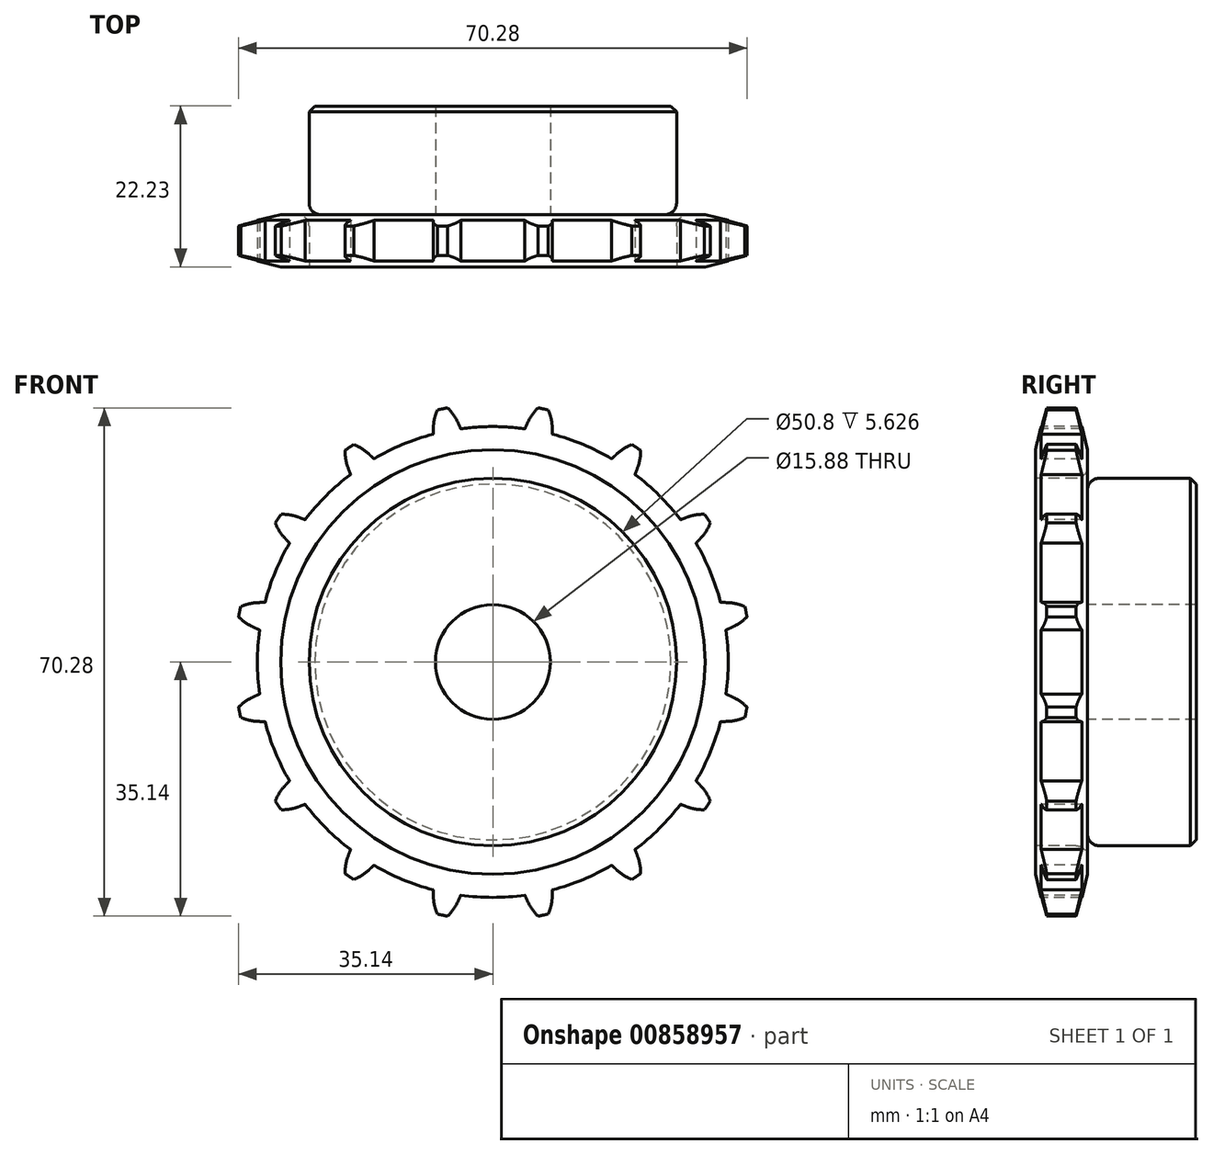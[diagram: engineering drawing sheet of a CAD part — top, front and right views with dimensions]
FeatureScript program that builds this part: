
annotation { "Feature Type Name" : "Feature", "Feature Type Description" : "" }
export const myFeature = defineFeature(function(context is Context, id is Id, definition is map)
    precondition{}
    {
        {
            var Q0;
            Q0=qCreatedBy(makeId("Right.planeOp"),FACE);
            var sketch = newSketch(context, id + "F0", { "sketchPlane" : qUnion([Q0])});
            skLineSegment(sketch, "E0", {"start": v(0, 0) * mm, "end": v(54, 0) * mm, "construction": true});
            skLineSegment(sketch, "E1.bottom", {"start": v(0, 35.69) * mm, "end": v(7.21, 35.69) * mm});
            skLineSegment(sketch, "E1.top", {"start": v(0, 7.94) * mm, "end": v(7.21, 7.94) * mm});
            skLineSegment(sketch, "E1.left", {"start": v(0, 35.69) * mm, "end": v(0, 7.94) * mm});
            skLineSegment(sketch, "E1.right", {"start": v(7.21, 35.69) * mm, "end": v(7.21, 7.94) * mm});
            skLineSegment(sketch, "E2.bottom", {"start": v(0, 7.94) * mm, "end": v(22.23, 7.94) * mm});
            skLineSegment(sketch, "E2.top", {"start": v(0, 25.4) * mm, "end": v(22.23, 25.4) * mm});
            skLineSegment(sketch, "E2.left", {"start": v(0, 7.94) * mm, "end": v(0, 25.4) * mm});
            skLineSegment(sketch, "E2.right", {"start": v(22.23, 7.94) * mm, "end": v(22.23, 25.4) * mm});
            skLineSegment(sketch, "E3.MirrorCS", {"start": v(0, -7.94) * mm, "end": v(7.21, -7.94) * mm});
            skLineSegment(sketch, "E4.MirrorCS", {"start": v(22.23, -7.94) * mm, "end": v(22.23, -25.4) * mm});
            skLineSegment(sketch, "E5.MirrorCS", {"start": v(0, -35.69) * mm, "end": v(0, -7.94) * mm});
            skLineSegment(sketch, "E6.MirrorCS", {"start": v(0, -25.4) * mm, "end": v(22.23, -25.4) * mm});
            skLineSegment(sketch, "E7.MirrorCS", {"start": v(0, -7.94) * mm, "end": v(22.23, -7.94) * mm});
            skLineSegment(sketch, "E8.MirrorCS", {"start": v(0, -7.94) * mm, "end": v(0, -25.4) * mm});
            skLineSegment(sketch, "E9.MirrorCS", {"start": v(0, -35.69) * mm, "end": v(7.21, -35.69) * mm});
            skLineSegment(sketch, "E10.MirrorCS", {"start": v(7.21, -35.69) * mm, "end": v(7.21, -7.94) * mm});
            skSolve(sketch);
        }
        {
            var Q0;
            {var subQ5=sQuery(id+"F0.wireOp",EDGE,"E2.left");Q0=makeQuery(id+"F0.imprint","IMPRINT",FACE,{"disambiguationData":[TD([[makeQuery(id+"F0.imprint","IMPRINT",EDGE,{"derivedFrom":subQ5}),-1.0]])]});}
            var Q1;
            {var subQ5=sQuery(id+"F0.wireOp",EDGE,"E2.right");Q1=makeQuery(id+"F0.imprint","IMPRINT",FACE,{"disambiguationData":[TD([[makeQuery(id+"F0.imprint","IMPRINT",EDGE,{"derivedFrom":subQ5}),1.0]])]});}
            var Q2;
            {var subQ0=sQuery(id+"F0.wireOp",EDGE,"E1.bottom");Q2=makeQuery(id+"F0.imprint","IMPRINT",FACE,{"disambiguationData":[TD([[makeQuery(id+"F0.imprint","IMPRINT",EDGE,{"derivedFrom":subQ0}),-1.0]])]});}
            var Q3;
            Q3=sQuery(id+"F0.wireOp",EDGE,"E0");
            revolve(context, id + "F1", {"surfaceOperationType" : NewSurfaceOperationType.NEW, "entities" : qUnion([Q0, Q1, Q2]), "axis" : qUnion([Q3]), "revolveType" : RevolveType.FULL});
        }
        {
            var Q0;
            Q0=makeQuery(id+"F1.opRevolve","SWEPT_EDGE",EDGE,{"disambiguationData":[OSD([sQuery(id+"F0.wireOp",EDGE,"E1.right"),sQuery(id+"F0.wireOp",EDGE,"E2.top")])]});
            fillet(context, id + "F2", {"entities" : qUnion([Q0]), "radius" : 1.59 * mm, "tangentPropagation" : true, "allowEdgeOverflow" : false});
        }
        {
            var Q0;
            Q0=makeQuery(id+"F1.opRevolve","SWEPT_EDGE",EDGE,{"disambiguationData":[OSD([sQuery(id+"F0.wireOp",EDGE,"E2.top"),sQuery(id+"F0.wireOp",EDGE,"E2.right")])]});
            chamfer(context, id + "F3", {"entities" : qUnion([Q0]), "width" : 0.8 * mm, "tangentPropagation" : true});
        }
        {
            var Q0;
            Q0=makeQuery(id+"F1.opRevolve","SWEPT_EDGE",EDGE,{"disambiguationData":[OSD([sQuery(id+"F0.wireOp",EDGE,"E1.bottom"),sQuery(id+"F0.wireOp",EDGE,"E1.left")])]});
            var Q1;
            Q1=makeQuery(id+"F1.opRevolve","SWEPT_EDGE",EDGE,{"disambiguationData":[OSD([sQuery(id+"F0.wireOp",EDGE,"E1.bottom"),sQuery(id+"F0.wireOp",EDGE,"E1.right")])]});
            chamfer(context, id + "F4", {"entities" : qUnion([Q0, Q1]), "chamferType" : ChamferType.TWO_OFFSETS, "width1" : 6.35 * mm, "oppositeDirection" : false, "width2" : 1.57 * mm, "tangentPropagation" : true});
        }
        {
            var Q0;
            Q0=makeQuery(id+"F1.opRevolve","SWEPT_FACE",FACE,{"disambiguationData":[OSD([sQuery(id+"F0.wireOp",EDGE,"E1.left"),sQuery(id+"F0.wireOp",EDGE,"E2.left")])]});
            var sketch = newSketch(context, id + "F5", { "sketchPlane" : qUnion([Q0])});
            skCircle(sketch, "E11", {"center": v(0, 0) * mm, "radius": 32.55 * mm});
            skLineSegment(sketch, "E12", {"start": v(0, 0) * mm, "end": v(0, 32.55) * mm, "construction": true});
            skLineSegment(sketch, "E13", {"start": v(0, 32.55) * mm, "end": v(36.9, 32.55) * mm, "construction": true});
            skLineSegment(sketch, "E14", {"start": v(0, 32.55) * mm, "end": v(5, 36.56) * mm, "construction": true});
            skLineSegment(sketch, "E15", {"start": v(5, 36.56) * mm, "end": v(-4.46, 32.3) * mm, "construction": true});
            skLineSegment(sketch, "E16", {"start": v(-4.46, 32.3) * mm, "end": v(-4.46, 32.3) * mm});
            skLineSegment(sketch, "E17", {"start": v(0, 0) * mm, "end": v(-7.13, 35.85) * mm, "construction": true});
            skArc(sketch, "E18", {"start": v(-7.13, 35.85) * mm, "mid": v(-15.87, 26.15) * mm, "end": v(-4.82, 33.1) * mm, "construction": true});
            skArc(sketch, "E19", {"start": v(-4.82, 33.1) * mm, "mid": v(-5.78, 34.63) * mm, "end": v(-7.13, 35.85) * mm});
            skLineSegment(sketch, "E20", {"start": v(-4.46, 32.3) * mm, "end": v(-4.82, 33.1) * mm});
            skLineSegment(sketch, "E21.MirrorCS", {"start": v(16.78, 7.56) * mm, "end": v(-7.6, 29.13) * mm, "construction": true});
            skArc(sketch, "E22", {"start": v(-4.46, 32.3) * mm, "mid": v(-3.84, 31.14) * mm, "end": v(-3.1, 30.07) * mm});
            skArc(sketch, "E23", {"start": v(-3.1, 30.07) * mm, "mid": v(13.83, 41.97) * mm, "end": v(-4.46, 32.3) * mm, "construction": true});
            skArc(sketch, "E24.MirrorCS", {"start": v(4.46, 32.3) * mm, "mid": v(3.84, 31.14) * mm, "end": v(3.1, 30.07) * mm});
            skLineSegment(sketch, "E25", {"start": v(-4.82, 33.1) * mm, "end": v(-4.46, 32.3) * mm});
            skArc(sketch, "E26.MirrorCS", {"start": v(-4.46, 32.3) * mm, "mid": v(-4, 31.07) * mm, "end": v(-3.7, 29.8) * mm});
            skArc(sketch, "E27.MirrorCS", {"start": v(-4.82, 33.1) * mm, "mid": v(-5.33, 34.84) * mm, "end": v(-5.34, 36.65) * mm, "construction": true});
            skArc(sketch, "E28.MirrorCS", {"start": v(-4.46, 32.3) * mm, "mid": v(-4, 31.07) * mm, "end": v(-3.7, 29.8) * mm, "construction": true});
            skCircle(sketch, "E29.MirrorC", {"center": v(-7.6, 29.13) * mm, "radius": 3.96 * mm, "construction": true});
            skArc(sketch, "E30.MirrorCS", {"start": v(4.82, 33.1) * mm, "mid": v(5.78, 34.63) * mm, "end": v(7.13, 35.85) * mm});
            skLineSegment(sketch, "E31.MirrorCS", {"start": v(4.82, 33.1) * mm, "end": v(4.46, 32.3) * mm});
            skArc(sketch, "E32", {"start": v(-3.1, 30.07) * mm, "mid": v(-1.31, 28.81) * mm, "end": v(0.86, 28.68) * mm});
            skArc(sketch, "E33", {"start": v(3.1, 30.07) * mm, "mid": v(0, 36.51) * mm, "end": v(-3.1, 30.07) * mm, "construction": true});
            skArc(sketch, "E34", {"start": v(0.86, 28.68) * mm, "mid": v(2.1, 29.19) * mm, "end": v(3.1, 30.07) * mm});
            skArc(sketch, "E35.1.0", {"start": v(-26.26, -20.72) * mm, "mid": v(-27.1, -22.33) * mm, "end": v(-27.48, -24.1) * mm});
            skLineSegment(sketch, "E35.1.1", {"start": v(-26.26, -20.72) * mm, "end": v(-25.74, -20) * mm});
            skArc(sketch, "E35.1.2", {"start": v(-25.74, -20) * mm, "mid": v(-25.05, -18.9) * mm, "end": v(-24.5, -17.71) * mm});
            skArc(sketch, "E35.2.0", {"start": v(31.07, -12.38) * mm, "mid": v(32.89, -12.3) * mm, "end": v(34.61, -11.75) * mm});
            skLineSegment(sketch, "E35.2.1", {"start": v(31.07, -12.38) * mm, "end": v(30.2, -12.3) * mm});
            skArc(sketch, "E35.2.2", {"start": v(30.2, -12.3) * mm, "mid": v(28.9, -12.24) * mm, "end": v(27.59, -12.36) * mm});
            skArc(sketch, "E36.1.0", {"start": v(-17.12, 28.74) * mm, "mid": v(-18.25, 30.15) * mm, "end": v(-18.96, 31.82) * mm, "construction": true});
            skArc(sketch, "E36.1.1", {"start": v(-16.48, 28.14) * mm, "mid": v(-15.58, 27.18) * mm, "end": v(-14.81, 26.12) * mm, "construction": true});
            skArc(sketch, "E36.1.2", {"start": v(-17.12, 28.74) * mm, "mid": v(-18.6, 29.79) * mm, "end": v(-20.3, 30.4) * mm});
            skLineSegment(sketch, "E36.1.3", {"start": v(-17.12, 28.74) * mm, "end": v(-16.48, 28.14) * mm});
            skArc(sketch, "E36.1.4", {"start": v(-16.48, 28.14) * mm, "mid": v(-15.47, 27.3) * mm, "end": v(-14.36, 26.6) * mm});
            skArc(sketch, "E36.1.5", {"start": v(-14.36, 26.6) * mm, "mid": v(-12.24, 26.12) * mm, "end": v(-10.18, 26.83) * mm});
            skArc(sketch, "E36.1.6", {"start": v(-10.18, 26.83) * mm, "mid": v(-9.23, 27.77) * mm, "end": v(-8.65, 28.96) * mm});
            skArc(sketch, "E36.1.7", {"start": v(-8.24, 31.55) * mm, "mid": v(-8.37, 30.24) * mm, "end": v(-8.65, 28.96) * mm});
            skLineSegment(sketch, "E36.1.8", {"start": v(-8.22, 32.42) * mm, "end": v(-8.24, 31.55) * mm});
            skArc(sketch, "E36.1.9", {"start": v(-8.22, 32.42) * mm, "mid": v(-7.91, 34.21) * mm, "end": v(-7.13, 35.85) * mm});
            skArc(sketch, "E36.2.0", {"start": v(-26.8, 20) * mm, "mid": v(-28.4, 20.87) * mm, "end": v(-29.7, 22.14) * mm, "construction": true});
            skArc(sketch, "E36.2.1", {"start": v(-26, 19.69) * mm, "mid": v(-24.8, 19.15) * mm, "end": v(-23.68, 18.46) * mm, "construction": true});
            skArc(sketch, "E36.2.2", {"start": v(-26.8, 20) * mm, "mid": v(-28.58, 20.4) * mm, "end": v(-30.4, 20.3) * mm});
            skLineSegment(sketch, "E36.2.3", {"start": v(-26.8, 20) * mm, "end": v(-26, 19.69) * mm});
            skArc(sketch, "E36.2.4", {"start": v(-26, 19.69) * mm, "mid": v(-24.74, 19.3) * mm, "end": v(-23.45, 19.08) * mm});
            skArc(sketch, "E36.2.5", {"start": v(-23.45, 19.08) * mm, "mid": v(-21.3, 19.45) * mm, "end": v(-19.67, 20.9) * mm});
            skArc(sketch, "E36.2.6", {"start": v(-19.67, 20.9) * mm, "mid": v(-19.16, 22.12) * mm, "end": v(-19.08, 23.45) * mm});
            skArc(sketch, "E36.2.7", {"start": v(-19.69, 26) * mm, "mid": v(-19.3, 24.74) * mm, "end": v(-19.08, 23.45) * mm});
            skLineSegment(sketch, "E36.2.8", {"start": v(-20, 26.8) * mm, "end": v(-19.69, 26) * mm});
            skArc(sketch, "E36.2.9", {"start": v(-20, 26.8) * mm, "mid": v(-20.4, 28.58) * mm, "end": v(-20.3, 30.4) * mm});
            skArc(sketch, "E36.3.0", {"start": v(-32.42, 8.22) * mm, "mid": v(-34.23, 8.41) * mm, "end": v(-35.9, 9.1) * mm, "construction": true});
            skArc(sketch, "E36.3.1", {"start": v(-31.55, 8.24) * mm, "mid": v(-30.24, 8.2) * mm, "end": v(-28.94, 8) * mm, "construction": true});
            skArc(sketch, "E36.3.2", {"start": v(-32.42, 8.22) * mm, "mid": v(-34.21, 7.91) * mm, "end": v(-35.85, 7.13) * mm});
            skLineSegment(sketch, "E36.3.3", {"start": v(-32.42, 8.22) * mm, "end": v(-31.55, 8.24) * mm});
            skArc(sketch, "E36.3.4", {"start": v(-31.55, 8.24) * mm, "mid": v(-30.24, 8.37) * mm, "end": v(-28.96, 8.65) * mm});
            skArc(sketch, "E36.3.5", {"start": v(-28.96, 8.65) * mm, "mid": v(-27.12, 9.81) * mm, "end": v(-26.17, 11.77) * mm});
            skArc(sketch, "E36.3.6", {"start": v(-26.17, 11.77) * mm, "mid": v(-26.16, 13.1) * mm, "end": v(-26.6, 14.36) * mm});
            skArc(sketch, "E36.3.7", {"start": v(-28.14, 16.48) * mm, "mid": v(-27.3, 15.47) * mm, "end": v(-26.6, 14.36) * mm});
            skLineSegment(sketch, "E36.3.8", {"start": v(-28.74, 17.12) * mm, "end": v(-28.14, 16.48) * mm});
            skArc(sketch, "E36.3.9", {"start": v(-28.74, 17.12) * mm, "mid": v(-29.79, 18.6) * mm, "end": v(-30.4, 20.3) * mm});
            skArc(sketch, "E36.4.0", {"start": v(-33.1, -4.82) * mm, "mid": v(-34.84, -5.33) * mm, "end": v(-36.65, -5.34) * mm, "construction": true});
            skArc(sketch, "E36.4.1", {"start": v(-32.3, -4.46) * mm, "mid": v(-31.07, -4) * mm, "end": v(-29.8, -3.7) * mm, "construction": true});
            skArc(sketch, "E36.4.2", {"start": v(-33.1, -4.82) * mm, "mid": v(-34.63, -5.78) * mm, "end": v(-35.85, -7.13) * mm});
            skLineSegment(sketch, "E36.4.3", {"start": v(-33.1, -4.82) * mm, "end": v(-32.3, -4.46) * mm});
            skArc(sketch, "E36.4.4", {"start": v(-32.3, -4.46) * mm, "mid": v(-31.14, -3.84) * mm, "end": v(-30.07, -3.1) * mm});
            skArc(sketch, "E36.4.5", {"start": v(-30.07, -3.1) * mm, "mid": v(-28.81, -1.31) * mm, "end": v(-28.68, 0.86) * mm});
            skArc(sketch, "E36.4.6", {"start": v(-28.68, 0.86) * mm, "mid": v(-29.19, 2.1) * mm, "end": v(-30.07, 3.1) * mm});
            skArc(sketch, "E36.4.7", {"start": v(-32.3, 4.46) * mm, "mid": v(-31.14, 3.84) * mm, "end": v(-30.07, 3.1) * mm});
            skLineSegment(sketch, "E36.4.8", {"start": v(-33.1, 4.82) * mm, "end": v(-32.3, 4.46) * mm});
            skArc(sketch, "E36.4.9", {"start": v(-33.1, 4.82) * mm, "mid": v(-34.63, 5.78) * mm, "end": v(-35.85, 7.13) * mm});
            skArc(sketch, "E36.5.0", {"start": v(-28.74, -17.12) * mm, "mid": v(-30.15, -18.25) * mm, "end": v(-31.82, -18.96) * mm, "construction": true});
            skArc(sketch, "E36.5.1", {"start": v(-28.14, -16.48) * mm, "mid": v(-27.18, -15.58) * mm, "end": v(-26.12, -14.81) * mm, "construction": true});
            skArc(sketch, "E36.5.2", {"start": v(-28.74, -17.12) * mm, "mid": v(-29.79, -18.6) * mm, "end": v(-30.4, -20.3) * mm});
            skLineSegment(sketch, "E36.5.3", {"start": v(-28.74, -17.12) * mm, "end": v(-28.14, -16.48) * mm});
            skArc(sketch, "E36.5.4", {"start": v(-28.14, -16.48) * mm, "mid": v(-27.3, -15.47) * mm, "end": v(-26.6, -14.36) * mm});
            skArc(sketch, "E36.5.5", {"start": v(-26.6, -14.36) * mm, "mid": v(-26.12, -12.24) * mm, "end": v(-26.83, -10.18) * mm});
            skArc(sketch, "E36.5.6", {"start": v(-26.83, -10.18) * mm, "mid": v(-27.77, -9.23) * mm, "end": v(-28.96, -8.65) * mm});
            skArc(sketch, "E36.5.7", {"start": v(-31.55, -8.24) * mm, "mid": v(-30.24, -8.37) * mm, "end": v(-28.96, -8.65) * mm});
            skLineSegment(sketch, "E36.5.8", {"start": v(-32.42, -8.22) * mm, "end": v(-31.55, -8.24) * mm});
            skArc(sketch, "E36.5.9", {"start": v(-32.42, -8.22) * mm, "mid": v(-34.21, -7.91) * mm, "end": v(-35.85, -7.13) * mm});
            skArc(sketch, "E36.6.0", {"start": v(-20, -26.8) * mm, "mid": v(-20.87, -28.4) * mm, "end": v(-22.14, -29.7) * mm, "construction": true});
            skArc(sketch, "E36.6.1", {"start": v(-19.69, -26) * mm, "mid": v(-19.15, -24.8) * mm, "end": v(-18.46, -23.68) * mm, "construction": true});
            skArc(sketch, "E36.6.2", {"start": v(-20, -26.8) * mm, "mid": v(-20.4, -28.58) * mm, "end": v(-20.3, -30.4) * mm});
            skLineSegment(sketch, "E36.6.3", {"start": v(-20, -26.8) * mm, "end": v(-19.69, -26) * mm});
            skArc(sketch, "E36.6.4", {"start": v(-19.69, -26) * mm, "mid": v(-19.3, -24.74) * mm, "end": v(-19.08, -23.45) * mm});
            skArc(sketch, "E36.6.5", {"start": v(-19.08, -23.45) * mm, "mid": v(-19.45, -21.3) * mm, "end": v(-20.9, -19.67) * mm});
            skArc(sketch, "E36.6.6", {"start": v(-20.9, -19.67) * mm, "mid": v(-22.12, -19.16) * mm, "end": v(-23.45, -19.08) * mm});
            skArc(sketch, "E36.6.7", {"start": v(-26, -19.69) * mm, "mid": v(-24.74, -19.3) * mm, "end": v(-23.45, -19.08) * mm});
            skLineSegment(sketch, "E36.6.8", {"start": v(-26.8, -20) * mm, "end": v(-26, -19.69) * mm});
            skArc(sketch, "E36.6.9", {"start": v(-26.8, -20) * mm, "mid": v(-28.58, -20.4) * mm, "end": v(-30.4, -20.3) * mm});
            skArc(sketch, "E36.7.0", {"start": v(-8.22, -32.42) * mm, "mid": v(-8.41, -34.23) * mm, "end": v(-9.1, -35.9) * mm, "construction": true});
            skArc(sketch, "E36.7.1", {"start": v(-8.24, -31.55) * mm, "mid": v(-8.2, -30.24) * mm, "end": v(-8, -28.94) * mm, "construction": true});
            skArc(sketch, "E36.7.2", {"start": v(-8.22, -32.42) * mm, "mid": v(-7.91, -34.21) * mm, "end": v(-7.13, -35.85) * mm});
            skLineSegment(sketch, "E36.7.3", {"start": v(-8.22, -32.42) * mm, "end": v(-8.24, -31.55) * mm});
            skArc(sketch, "E36.7.4", {"start": v(-8.24, -31.55) * mm, "mid": v(-8.37, -30.24) * mm, "end": v(-8.65, -28.96) * mm});
            skArc(sketch, "E36.7.5", {"start": v(-8.65, -28.96) * mm, "mid": v(-9.81, -27.12) * mm, "end": v(-11.77, -26.17) * mm});
            skArc(sketch, "E36.7.6", {"start": v(-11.77, -26.17) * mm, "mid": v(-13.1, -26.16) * mm, "end": v(-14.36, -26.6) * mm});
            skArc(sketch, "E36.7.7", {"start": v(-16.48, -28.14) * mm, "mid": v(-15.47, -27.3) * mm, "end": v(-14.36, -26.6) * mm});
            skLineSegment(sketch, "E36.7.8", {"start": v(-17.12, -28.74) * mm, "end": v(-16.48, -28.14) * mm});
            skArc(sketch, "E36.7.9", {"start": v(-17.12, -28.74) * mm, "mid": v(-18.6, -29.79) * mm, "end": v(-20.3, -30.4) * mm});
            skArc(sketch, "E36.8.0", {"start": v(4.82, -33.1) * mm, "mid": v(5.33, -34.84) * mm, "end": v(5.34, -36.65) * mm, "construction": true});
            skArc(sketch, "E36.8.1", {"start": v(4.46, -32.3) * mm, "mid": v(4, -31.07) * mm, "end": v(3.7, -29.8) * mm, "construction": true});
            skArc(sketch, "E36.8.2", {"start": v(4.82, -33.1) * mm, "mid": v(5.78, -34.63) * mm, "end": v(7.13, -35.85) * mm});
            skLineSegment(sketch, "E36.8.3", {"start": v(4.82, -33.1) * mm, "end": v(4.46, -32.3) * mm});
            skArc(sketch, "E36.8.4", {"start": v(4.46, -32.3) * mm, "mid": v(3.84, -31.14) * mm, "end": v(3.1, -30.07) * mm});
            skArc(sketch, "E36.8.5", {"start": v(3.1, -30.07) * mm, "mid": v(1.31, -28.81) * mm, "end": v(-0.86, -28.68) * mm});
            skArc(sketch, "E36.8.6", {"start": v(-0.86, -28.68) * mm, "mid": v(-2.1, -29.19) * mm, "end": v(-3.1, -30.07) * mm});
            skArc(sketch, "E36.8.7", {"start": v(-4.46, -32.3) * mm, "mid": v(-3.84, -31.14) * mm, "end": v(-3.1, -30.07) * mm});
            skLineSegment(sketch, "E36.8.8", {"start": v(-4.82, -33.1) * mm, "end": v(-4.46, -32.3) * mm});
            skArc(sketch, "E36.8.9", {"start": v(-4.82, -33.1) * mm, "mid": v(-5.78, -34.63) * mm, "end": v(-7.13, -35.85) * mm});
            skArc(sketch, "E36.9.0", {"start": v(17.12, -28.74) * mm, "mid": v(18.25, -30.15) * mm, "end": v(18.96, -31.82) * mm, "construction": true});
            skArc(sketch, "E36.9.1", {"start": v(16.48, -28.14) * mm, "mid": v(15.58, -27.18) * mm, "end": v(14.81, -26.12) * mm, "construction": true});
            skArc(sketch, "E36.9.2", {"start": v(17.12, -28.74) * mm, "mid": v(18.6, -29.79) * mm, "end": v(20.3, -30.4) * mm});
            skLineSegment(sketch, "E36.9.3", {"start": v(17.12, -28.74) * mm, "end": v(16.48, -28.14) * mm});
            skArc(sketch, "E36.9.4", {"start": v(16.48, -28.14) * mm, "mid": v(15.47, -27.3) * mm, "end": v(14.36, -26.6) * mm});
            skArc(sketch, "E36.9.5", {"start": v(14.36, -26.6) * mm, "mid": v(12.24, -26.12) * mm, "end": v(10.18, -26.83) * mm});
            skArc(sketch, "E36.9.6", {"start": v(10.18, -26.83) * mm, "mid": v(9.23, -27.77) * mm, "end": v(8.65, -28.96) * mm});
            skArc(sketch, "E36.9.7", {"start": v(8.24, -31.55) * mm, "mid": v(8.37, -30.24) * mm, "end": v(8.65, -28.96) * mm});
            skLineSegment(sketch, "E36.9.8", {"start": v(8.22, -32.42) * mm, "end": v(8.24, -31.55) * mm});
            skArc(sketch, "E36.9.9", {"start": v(8.22, -32.42) * mm, "mid": v(7.91, -34.21) * mm, "end": v(7.13, -35.85) * mm});
            skArc(sketch, "E36.10.0", {"start": v(26.8, -20) * mm, "mid": v(28.4, -20.87) * mm, "end": v(29.7, -22.14) * mm, "construction": true});
            skArc(sketch, "E36.10.1", {"start": v(26, -19.69) * mm, "mid": v(24.8, -19.15) * mm, "end": v(23.68, -18.46) * mm, "construction": true});
            skArc(sketch, "E36.10.2", {"start": v(26.8, -20) * mm, "mid": v(28.58, -20.4) * mm, "end": v(30.4, -20.3) * mm});
            skLineSegment(sketch, "E36.10.3", {"start": v(26.8, -20) * mm, "end": v(26, -19.69) * mm});
            skArc(sketch, "E36.10.4", {"start": v(26, -19.69) * mm, "mid": v(24.74, -19.3) * mm, "end": v(23.45, -19.08) * mm});
            skArc(sketch, "E36.10.5", {"start": v(23.45, -19.08) * mm, "mid": v(21.3, -19.45) * mm, "end": v(19.67, -20.9) * mm});
            skArc(sketch, "E36.10.6", {"start": v(19.67, -20.9) * mm, "mid": v(19.16, -22.12) * mm, "end": v(19.08, -23.45) * mm});
            skArc(sketch, "E36.10.7", {"start": v(19.69, -26) * mm, "mid": v(19.3, -24.74) * mm, "end": v(19.08, -23.45) * mm});
            skLineSegment(sketch, "E36.10.8", {"start": v(20, -26.8) * mm, "end": v(19.69, -26) * mm});
            skArc(sketch, "E36.10.9", {"start": v(20, -26.8) * mm, "mid": v(20.4, -28.58) * mm, "end": v(20.3, -30.4) * mm});
            skArc(sketch, "E36.11.0", {"start": v(32.42, -8.22) * mm, "mid": v(34.23, -8.41) * mm, "end": v(35.9, -9.1) * mm, "construction": true});
            skArc(sketch, "E36.11.1", {"start": v(31.55, -8.24) * mm, "mid": v(30.24, -8.2) * mm, "end": v(28.94, -8) * mm, "construction": true});
            skArc(sketch, "E36.11.2", {"start": v(32.42, -8.22) * mm, "mid": v(34.21, -7.91) * mm, "end": v(35.85, -7.13) * mm});
            skLineSegment(sketch, "E36.11.3", {"start": v(32.42, -8.22) * mm, "end": v(31.55, -8.24) * mm});
            skArc(sketch, "E36.11.4", {"start": v(31.55, -8.24) * mm, "mid": v(30.24, -8.37) * mm, "end": v(28.96, -8.65) * mm});
            skArc(sketch, "E36.11.5", {"start": v(28.96, -8.65) * mm, "mid": v(27.12, -9.81) * mm, "end": v(26.17, -11.77) * mm});
            skArc(sketch, "E36.11.6", {"start": v(26.17, -11.77) * mm, "mid": v(26.16, -13.1) * mm, "end": v(26.6, -14.36) * mm});
            skArc(sketch, "E36.11.7", {"start": v(28.14, -16.48) * mm, "mid": v(27.3, -15.47) * mm, "end": v(26.6, -14.36) * mm});
            skLineSegment(sketch, "E36.11.8", {"start": v(28.74, -17.12) * mm, "end": v(28.14, -16.48) * mm});
            skArc(sketch, "E36.11.9", {"start": v(28.74, -17.12) * mm, "mid": v(29.79, -18.6) * mm, "end": v(30.4, -20.3) * mm});
            skArc(sketch, "E36.12.0", {"start": v(33.1, 4.82) * mm, "mid": v(34.84, 5.33) * mm, "end": v(36.65, 5.34) * mm, "construction": true});
            skArc(sketch, "E36.12.1", {"start": v(32.3, 4.46) * mm, "mid": v(31.07, 4) * mm, "end": v(29.8, 3.7) * mm, "construction": true});
            skArc(sketch, "E36.12.2", {"start": v(33.1, 4.82) * mm, "mid": v(34.63, 5.78) * mm, "end": v(35.85, 7.13) * mm});
            skLineSegment(sketch, "E36.12.3", {"start": v(33.1, 4.82) * mm, "end": v(32.3, 4.46) * mm});
            skArc(sketch, "E36.12.4", {"start": v(32.3, 4.46) * mm, "mid": v(31.14, 3.84) * mm, "end": v(30.07, 3.1) * mm});
            skArc(sketch, "E36.12.5", {"start": v(30.07, 3.1) * mm, "mid": v(28.81, 1.31) * mm, "end": v(28.68, -0.86) * mm});
            skArc(sketch, "E36.12.6", {"start": v(28.68, -0.86) * mm, "mid": v(29.19, -2.1) * mm, "end": v(30.07, -3.1) * mm});
            skArc(sketch, "E36.12.7", {"start": v(32.3, -4.46) * mm, "mid": v(31.14, -3.84) * mm, "end": v(30.07, -3.1) * mm});
            skLineSegment(sketch, "E36.12.8", {"start": v(33.1, -4.82) * mm, "end": v(32.3, -4.46) * mm});
            skArc(sketch, "E36.12.9", {"start": v(33.1, -4.82) * mm, "mid": v(34.63, -5.78) * mm, "end": v(35.85, -7.13) * mm});
            skArc(sketch, "E36.13.0", {"start": v(28.74, 17.12) * mm, "mid": v(30.15, 18.25) * mm, "end": v(31.82, 18.96) * mm, "construction": true});
            skArc(sketch, "E36.13.1", {"start": v(28.14, 16.48) * mm, "mid": v(27.18, 15.58) * mm, "end": v(26.12, 14.81) * mm, "construction": true});
            skArc(sketch, "E36.13.2", {"start": v(28.74, 17.12) * mm, "mid": v(29.79, 18.6) * mm, "end": v(30.4, 20.3) * mm});
            skLineSegment(sketch, "E36.13.3", {"start": v(28.74, 17.12) * mm, "end": v(28.14, 16.48) * mm});
            skArc(sketch, "E36.13.4", {"start": v(28.14, 16.48) * mm, "mid": v(27.3, 15.47) * mm, "end": v(26.6, 14.36) * mm});
            skArc(sketch, "E36.13.5", {"start": v(26.6, 14.36) * mm, "mid": v(26.12, 12.24) * mm, "end": v(26.83, 10.18) * mm});
            skArc(sketch, "E36.13.6", {"start": v(26.83, 10.18) * mm, "mid": v(27.77, 9.23) * mm, "end": v(28.96, 8.65) * mm});
            skArc(sketch, "E36.13.7", {"start": v(31.55, 8.24) * mm, "mid": v(30.24, 8.37) * mm, "end": v(28.96, 8.65) * mm});
            skLineSegment(sketch, "E36.13.8", {"start": v(32.42, 8.22) * mm, "end": v(31.55, 8.24) * mm});
            skArc(sketch, "E36.13.9", {"start": v(32.42, 8.22) * mm, "mid": v(34.21, 7.91) * mm, "end": v(35.85, 7.13) * mm});
            skArc(sketch, "E36.14.0", {"start": v(20, 26.8) * mm, "mid": v(20.87, 28.4) * mm, "end": v(22.14, 29.7) * mm, "construction": true});
            skArc(sketch, "E36.14.1", {"start": v(19.69, 26) * mm, "mid": v(19.15, 24.8) * mm, "end": v(18.46, 23.68) * mm, "construction": true});
            skArc(sketch, "E36.14.2", {"start": v(20, 26.8) * mm, "mid": v(20.4, 28.58) * mm, "end": v(20.3, 30.4) * mm});
            skLineSegment(sketch, "E36.14.3", {"start": v(20, 26.8) * mm, "end": v(19.69, 26) * mm});
            skArc(sketch, "E36.14.4", {"start": v(19.69, 26) * mm, "mid": v(19.3, 24.74) * mm, "end": v(19.08, 23.45) * mm});
            skArc(sketch, "E36.14.5", {"start": v(19.08, 23.45) * mm, "mid": v(19.45, 21.3) * mm, "end": v(20.9, 19.67) * mm});
            skArc(sketch, "E36.14.6", {"start": v(20.9, 19.67) * mm, "mid": v(22.12, 19.16) * mm, "end": v(23.45, 19.08) * mm});
            skArc(sketch, "E36.14.7", {"start": v(26, 19.69) * mm, "mid": v(24.74, 19.3) * mm, "end": v(23.45, 19.08) * mm});
            skLineSegment(sketch, "E36.14.8", {"start": v(26.8, 20) * mm, "end": v(26, 19.69) * mm});
            skArc(sketch, "E36.14.9", {"start": v(26.8, 20) * mm, "mid": v(28.58, 20.4) * mm, "end": v(30.4, 20.3) * mm});
            skArc(sketch, "E36.15.0", {"start": v(8.22, 32.42) * mm, "mid": v(8.41, 34.23) * mm, "end": v(9.1, 35.9) * mm, "construction": true});
            skArc(sketch, "E36.15.1", {"start": v(8.24, 31.55) * mm, "mid": v(8.2, 30.24) * mm, "end": v(8, 28.94) * mm, "construction": true});
            skArc(sketch, "E36.15.2", {"start": v(8.22, 32.42) * mm, "mid": v(7.91, 34.21) * mm, "end": v(7.13, 35.85) * mm});
            skLineSegment(sketch, "E36.15.3", {"start": v(8.22, 32.42) * mm, "end": v(8.24, 31.55) * mm});
            skArc(sketch, "E36.15.4", {"start": v(8.24, 31.55) * mm, "mid": v(8.37, 30.24) * mm, "end": v(8.65, 28.96) * mm});
            skArc(sketch, "E36.15.5", {"start": v(8.65, 28.96) * mm, "mid": v(9.81, 27.12) * mm, "end": v(11.77, 26.17) * mm});
            skArc(sketch, "E36.15.6", {"start": v(11.77, 26.17) * mm, "mid": v(13.1, 26.16) * mm, "end": v(14.36, 26.6) * mm});
            skArc(sketch, "E36.15.7", {"start": v(16.48, 28.14) * mm, "mid": v(15.47, 27.3) * mm, "end": v(14.36, 26.6) * mm});
            skLineSegment(sketch, "E36.15.8", {"start": v(17.12, 28.74) * mm, "end": v(16.48, 28.14) * mm});
            skArc(sketch, "E36.15.9", {"start": v(17.12, 28.74) * mm, "mid": v(18.6, 29.79) * mm, "end": v(20.3, 30.4) * mm});
            skSolve(sketch);
        }
        {
            var Q0;
            Q0 = qSketchRegion(id + "F5", true);
            extrude(context, id + "F6", {"entities" : qUnion([Q0]), "operationType" : NewBodyOperationType.INTERSECT, "endBound" : BoundingType.THROUGH_ALL, "oppositeDirection" : true, "depth" : 25.4 * mm, "offsetDistance" : 25.4 * mm});
        }
    });
